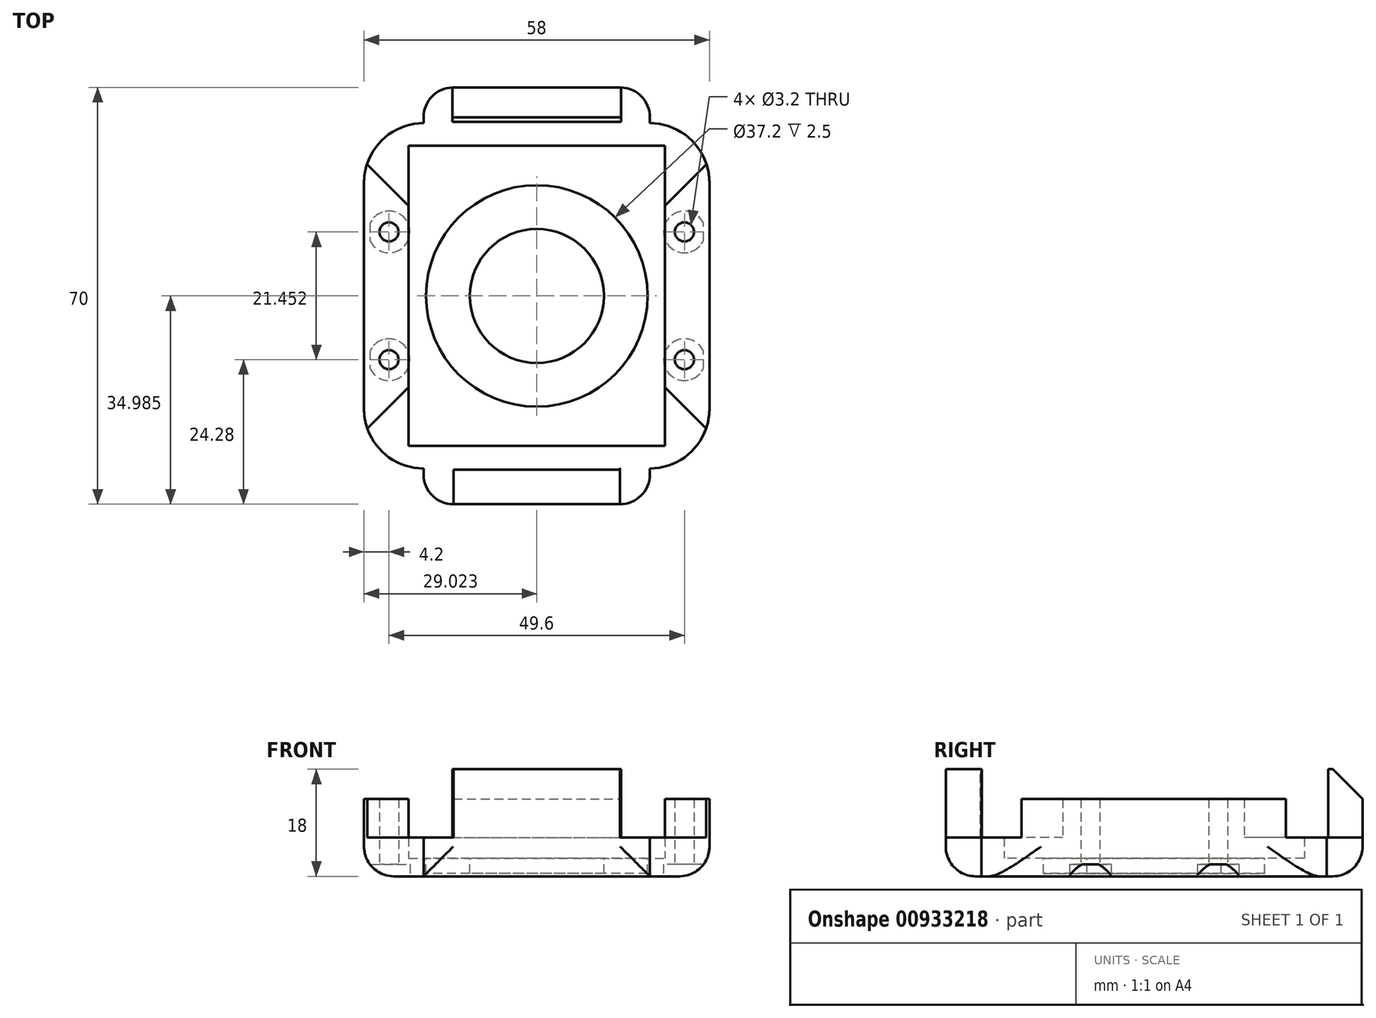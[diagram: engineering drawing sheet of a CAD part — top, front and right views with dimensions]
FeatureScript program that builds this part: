
annotation { "Feature Type Name" : "Feature", "Feature Type Description" : "" }
export const myFeature = defineFeature(function(context is Context, id is Id, definition is map)
    precondition{}
    {
        {
            var Q0;
            Q0=qCreatedBy(makeId("Top.planeOp"),FACE);
            var sketch = newSketch(context, id + "F0", { "sketchPlane" : qUnion([Q0])});
            skPoint(sketch, "E0.middle", {"position": v(-30.2, 30.2) * mm});
            skLineSegment(sketch, "E1", {"start": v(-30.2, 30.2) * mm, "end": v(-30.2, 55.4) * mm});
            skLineSegment(sketch, "E2", {"start": v(-30.2, 55.4) * mm, "end": v(-30.2, 59.2) * mm});
            skLineSegment(sketch, "E3", {"start": v(-30.2, 30.2) * mm, "end": v(-30.2, 5) * mm});
            skLineSegment(sketch, "E4", {"start": v(-30.2, 5) * mm, "end": v(-30.2, 1.2) * mm});
            skLineSegment(sketch, "E5", {"start": v(-30.2, 1.2) * mm, "end": v(-11.2, 1.2) * mm});
            skLineSegment(sketch, "E6", {"start": v(-1.2, 49.2) * mm, "end": v(-1.2, 11.2) * mm});
            skLineSegment(sketch, "E7", {"start": v(-11.2, 59.2) * mm, "end": v(-30.2, 59.2) * mm});
            skLineSegment(sketch, "E8", {"start": v(-8.68, 55.4) * mm, "end": v(-8.68, 5) * mm});
            skLineSegment(sketch, "E9.MirrorCS", {"start": v(-51.73, 55.4) * mm, "end": v(-51.73, 5) * mm});
            skLineSegment(sketch, "E10.MirrorCS", {"start": v(-30.2, 1.2) * mm, "end": v(-49.2, 1.2) * mm});
            skLineSegment(sketch, "E11.MirrorCS", {"start": v(-49.2, 59.2) * mm, "end": v(-30.2, 59.2) * mm});
            skLineSegment(sketch, "E12.MirrorCS", {"start": v(-59.2, 49.2) * mm, "end": v(-59.2, 11.2) * mm});
            skArc(sketch, "E13", {"start": v(-49.2, 59.2) * mm, "mid": v(-56.27, 56.27) * mm, "end": v(-59.2, 49.2) * mm});
            skArc(sketch, "E14", {"start": v(-1.2, 49.2) * mm, "mid": v(-4.13, 56.27) * mm, "end": v(-11.2, 59.2) * mm});
            skArc(sketch, "E15", {"start": v(-11.2, 1.2) * mm, "mid": v(-4.13, 4.13) * mm, "end": v(-1.2, 11.2) * mm});
            skArc(sketch, "E16", {"start": v(-59.2, 11.2) * mm, "mid": v(-56.27, 4.13) * mm, "end": v(-49.2, 1.2) * mm});
            skLineSegment(sketch, "E17", {"start": v(-51.73, 5) * mm, "end": v(-30.2, 5) * mm});
            skLineSegment(sketch, "E18", {"start": v(-30.2, 5) * mm, "end": v(-8.68, 5) * mm});
            skLineSegment(sketch, "E19", {"start": v(-51.73, 55.4) * mm, "end": v(-30.2, 55.4) * mm});
            skLineSegment(sketch, "E20", {"start": v(-8.68, 55.4) * mm, "end": v(-30.2, 55.4) * mm});
            skSolve(sketch);
        }
        {
            var Q0;
            Q0=makeQuery(id+"F0.imprint","IMPRINT",FACE,{"disambiguationData":[TD([[makeQuery(id+"F0.imprint","IMPRINT",EDGE,{"derivedFrom":sQuery(id+"F0.wireOp",EDGE,"E4")}),-1.0]])]});
            var Q1;
            Q1=makeQuery(id+"F0.imprint","IMPRINT",FACE,{"disambiguationData":[TD([[makeQuery(id+"F0.imprint","IMPRINT",EDGE,{"derivedFrom":sQuery(id+"F0.wireOp",EDGE,"GW4XANve-GKL7-1srf-qrfw-00KNjBr2ELYc")}),1.0]])]});
            var Q2;
            Q2=makeQuery(id+"F0.imprint","IMPRINT",FACE,{"disambiguationData":[TD([[makeQuery(id+"F0.imprint","IMPRINT",EDGE,{"derivedFrom":sQuery(id+"F0.wireOp",EDGE,"E5")}),1.0]])]});
            extrude(context, id + "F1", {"entities" : qUnion([Q0, Q1, Q2]), "depth" : 13 * mm, "offsetDistance" : 25 * mm});
        }
        {
            var Q0;
            Q0=makeQuery(id+"F1.opExtrude","CAP_EDGE",EDGE,{"disambiguationData":[OSD([sQuery(id+"F0.wireOp",EDGE,"E6")])],"isStart":true});
            var Q1;
            Q1=makeQuery(id+"F1.opExtrude","CAP_EDGE",EDGE,{"disambiguationData":[OSD([sQuery(id+"F0.wireOp",EDGE,"E12.MirrorCS")])],"isStart":true});
            fillet(context, id + "F2", {"entities" : qUnion([Q0, Q1]), "radius" : 5 * mm, "allowEdgeOverflow" : false});
        }
        {
            var Q0;
            Q0=makeQuery(id+"F0.imprint","IMPRINT",FACE,{"disambiguationData":[TD([[makeQuery(id+"F0.imprint","IMPRINT",EDGE,{"derivedFrom":sQuery(id+"F0.wireOp",EDGE,"E1")}),1.0]])]});
            var Q1;
            Q1=makeQuery(id+"F0.imprint","IMPRINT",FACE,{"disambiguationData":[TD([[makeQuery(id+"F0.imprint","IMPRINT",EDGE,{"derivedFrom":sQuery(id+"F0.wireOp",EDGE,"E1")}),-1.0]])]});
            extrude(context, id + "F3", {"entities" : qUnion([Q0, Q1]), "operationType" : NewBodyOperationType.ADD, "depth" : 3 * mm, "offsetDistance" : 25 * mm});
        }
        {
            var Q0;
            Q0=qCreatedBy(makeId("Top.planeOp"),FACE);
            var sketch = newSketch(context, id + "F4", { "sketchPlane" : qUnion([Q0])});
            skCircle(sketch, "E21", {"center": v(-60.36, 60) * mm, "radius": 3.5 * mm});
            skCircle(sketch, "E22", {"center": v(-60.36, 0) * mm, "radius": 3.5 * mm});
            skCircle(sketch, "E23", {"center": v(-0.4, 60) * mm, "radius": 3.5 * mm});
            skCircle(sketch, "E24", {"center": v(-0.4, 0) * mm, "radius": 3.5 * mm});
            skCircle(sketch, "E25", {"center": v(-60.36, 0) * mm, "radius": 1.6 * mm});
            skCircle(sketch, "E26", {"center": v(-60.36, 60) * mm, "radius": 1.6 * mm});
            skCircle(sketch, "E27", {"center": v(-0.4, 0) * mm, "radius": 1.6 * mm});
            skCircle(sketch, "E28", {"center": v(-0.4, 60) * mm, "radius": 1.6 * mm});
            skCircle(sketch, "E29", {"center": v(-5.4, 40.93) * mm, "radius": 1.6 * mm});
            skCircle(sketch, "E30", {"center": v(-5.4, 19.48) * mm, "radius": 1.6 * mm});
            skCircle(sketch, "E31", {"center": v(-55, 40.93) * mm, "radius": 1.6 * mm});
            skCircle(sketch, "E32", {"center": v(-55, 19.48) * mm, "radius": 1.6 * mm});
            skCircle(sketch, "E33", {"center": v(-55, 40.93) * mm, "radius": 3.5 * mm});
            skCircle(sketch, "E34", {"center": v(-55, 19.48) * mm, "radius": 3.5 * mm});
            skCircle(sketch, "E35", {"center": v(-5.4, 40.93) * mm, "radius": 3.5 * mm});
            skCircle(sketch, "E36", {"center": v(-5.4, 19.48) * mm, "radius": 3.5 * mm});
            skLineSegment(sketch, "E37", {"start": v(-29.99, 1.14) * mm, "end": v(-67.14, 1.14) * mm});
            skCircle(sketch, "E38", {"center": v(-9.99, 9.78) * mm, "radius": 4 * mm});
            skCircle(sketch, "E39", {"center": v(-9.99, 50.33) * mm, "radius": 4 * mm});
            skCircle(sketch, "E40", {"center": v(-50.56, 9.78) * mm, "radius": 4 * mm});
            skCircle(sketch, "E41", {"center": v(-50.56, 50.33) * mm, "radius": 4 * mm});
            skSolve(sketch);
        }
        {
            var Q0;
            Q0=makeQuery(id+"F4.imprint","IMPRINT",FACE,{"disambiguationData":[TD([[makeQuery(id+"F4.imprint","IMPRINT",EDGE,{"derivedFrom":sQuery(id+"F4.wireOp",EDGE,"E23")}),1.0]])]});
            var Q1;
            Q1=makeQuery(id+"F4.imprint","IMPRINT",FACE,{"disambiguationData":[TD([[makeQuery(id+"F4.imprint","IMPRINT",EDGE,{"derivedFrom":sQuery(id+"F4.wireOp",EDGE,"E21")}),1.0]])]});
            var Q2;
            Q2=makeQuery(id+"F4.imprint","IMPRINT",FACE,{"disambiguationData":[TD([[makeQuery(id+"F4.imprint","IMPRINT",EDGE,{"derivedFrom":sQuery(id+"F4.wireOp",EDGE,"E22")}),1.0]])]});
            var Q3;
            Q3=makeQuery(id+"F4.imprint","IMPRINT",FACE,{"disambiguationData":[TD([[makeQuery(id+"F4.imprint","IMPRINT",EDGE,{"derivedFrom":sQuery(id+"F4.wireOp",EDGE,"E24")}),1.0]])]});
            var Q4;
            Q4=makeQuery(id+"F4.imprint","IMPRINT",FACE,{"disambiguationData":[TD([[makeQuery(id+"F4.imprint","IMPRINT",EDGE,{"derivedFrom":sQuery(id+"F4.wireOp",EDGE,"E31")}),-1.0]])]});
            var Q5;
            Q5=makeQuery(id+"F4.imprint","IMPRINT",FACE,{"disambiguationData":[TD([[makeQuery(id+"F4.imprint","IMPRINT",EDGE,{"derivedFrom":sQuery(id+"F4.wireOp",EDGE,"E32")}),-1.0]])]});
            var Q6;
            Q6=makeQuery(id+"F4.imprint","IMPRINT",FACE,{"disambiguationData":[TD([[makeQuery(id+"F4.imprint","IMPRINT",EDGE,{"derivedFrom":sQuery(id+"F4.wireOp",EDGE,"E29")}),-1.0]])]});
            var Q7;
            Q7=makeQuery(id+"F4.imprint","IMPRINT",FACE,{"disambiguationData":[TD([[makeQuery(id+"F4.imprint","IMPRINT",EDGE,{"derivedFrom":sQuery(id+"F4.wireOp",EDGE,"E30")}),-1.0]])]});
            var Q8;
            Q8=sQuery(id+"F4.wireOp",EDGE,"E23");
            extrude(context, id + "F5", {"entities" : qUnion([Q0, Q1, Q2, Q3, Q4, Q5, Q6, Q7]), "operationType" : NewBodyOperationType.REMOVE, "surfaceEntities" : qUnion([Q8]), "depth" : 2 * mm, "offsetDistance" : 25 * mm});
        }
        {
            var Q0;
            Q0=makeQuery(id+"F4.imprint","IMPRINT",FACE,{"disambiguationData":[TD([[makeQuery(id+"F4.imprint","IMPRINT",EDGE,{"derivedFrom":sQuery(id+"F4.wireOp",EDGE,"E27")}),1.0]])]});
            var Q1;
            Q1=makeQuery(id+"F4.imprint","IMPRINT",FACE,{"disambiguationData":[TD([[makeQuery(id+"F4.imprint","IMPRINT",EDGE,{"derivedFrom":sQuery(id+"F4.wireOp",EDGE,"E28")}),1.0]])]});
            var Q2;
            Q2=makeQuery(id+"F4.imprint","IMPRINT",FACE,{"disambiguationData":[TD([[makeQuery(id+"F4.imprint","IMPRINT",EDGE,{"derivedFrom":sQuery(id+"F4.wireOp",EDGE,"E26")}),1.0]])]});
            var Q3;
            Q3=makeQuery(id+"F4.imprint","IMPRINT",FACE,{"disambiguationData":[TD([[makeQuery(id+"F4.imprint","IMPRINT",EDGE,{"derivedFrom":sQuery(id+"F4.wireOp",EDGE,"E25")}),1.0]])]});
            var Q4;
            Q4=makeQuery(id+"F4.imprint","IMPRINT",FACE,{"disambiguationData":[TD([[makeQuery(id+"F4.imprint","IMPRINT",EDGE,{"derivedFrom":sQuery(id+"F4.wireOp",EDGE,"E29")}),1.0]])]});
            var Q5;
            Q5=makeQuery(id+"F4.imprint","IMPRINT",FACE,{"disambiguationData":[TD([[makeQuery(id+"F4.imprint","IMPRINT",EDGE,{"derivedFrom":sQuery(id+"F4.wireOp",EDGE,"E30")}),1.0]])]});
            var Q6;
            Q6=makeQuery(id+"F4.imprint","IMPRINT",FACE,{"disambiguationData":[TD([[makeQuery(id+"F4.imprint","IMPRINT",EDGE,{"derivedFrom":sQuery(id+"F4.wireOp",EDGE,"E32")}),1.0]])]});
            var Q7;
            Q7=makeQuery(id+"F4.imprint","IMPRINT",FACE,{"disambiguationData":[TD([[makeQuery(id+"F4.imprint","IMPRINT",EDGE,{"derivedFrom":sQuery(id+"F4.wireOp",EDGE,"E31")}),1.0]])]});
            extrude(context, id + "F6", {"entities" : qUnion([Q0, Q1, Q2, Q3, Q4, Q5, Q6, Q7]), "operationType" : NewBodyOperationType.REMOVE, "depth" : 25 * mm, "offsetDistance" : 25 * mm});
        }
        {
            var Q0;
            Q0=makeQuery(id+"F3.opExtrude","CAP_FACE",FACE,{"disambiguationData":[OSD([sQuery(id+"F0.wireOp",EDGE,"piOKfCNf-9K0Y-vCMg-MYKp-rQM3WEvo7tjS"),sQuery(id+"F0.wireOp",EDGE,"E8"),sQuery(id+"F0.wireOp",EDGE,"WZ0sFQZI-nBvw-yqqw-dlFr-medNQ8aPjnrY"),sQuery(id+"F0.wireOp",EDGE,"af8eacb0-9355-44b9-9afd-123b7ccd3d5d11.MirrorCS"),sQuery(id+"F0.wireOp",EDGE,"E9.MirrorCS"),sQuery(id+"F0.wireOp",EDGE,"af8eacb0-9355-44b9-9afd-123b7ccd3d5d20.MirrorCS")])],"isStart":false});
            var sketch = newSketch(context, id + "F7", { "sketchPlane" : qUnion([Q0])});
            skCircle(sketch, "E42", {"center": v(-30.18, 30.19) * mm, "radius": 18.6 * mm});
            skCircle(sketch, "E43", {"center": v(-30.18, 30.19) * mm, "radius": 11.25 * mm});
            skSolve(sketch);
        }
        {
            var Q0;
            Q0=makeQuery(id+"F7.imprint","IMPRINT",FACE,{"disambiguationData":[TD([[makeQuery(id+"F7.imprint","IMPRINT",EDGE,{"derivedFrom":sQuery(id+"F7.wireOp",EDGE,"E42")}),1.0]])]});
            extrude(context, id + "F8", {"entities" : qUnion([Q0]), "operationType" : NewBodyOperationType.REMOVE, "oppositeDirection" : true, "depth" : 2.5 * mm, "offsetDistance" : 25 * mm});
        }
        {
            var Q0;
            Q0=makeQuery(id+"F4.imprint","IMPRINT",FACE,{"disambiguationData":[TD([[makeQuery(id+"F4.imprint","IMPRINT",EDGE,{"derivedFrom":sQuery(id+"F4.wireOp",EDGE,"E39")}),1.0]])]});
            var Q1;
            Q1=makeQuery(id+"F4.imprint","IMPRINT",FACE,{"disambiguationData":[TD([[makeQuery(id+"F4.imprint","IMPRINT",EDGE,{"derivedFrom":sQuery(id+"F4.wireOp",EDGE,"E41")}),1.0]])]});
            var Q2;
            Q2=makeQuery(id+"F4.imprint","IMPRINT",FACE,{"disambiguationData":[TD([[makeQuery(id+"F4.imprint","IMPRINT",EDGE,{"derivedFrom":sQuery(id+"F4.wireOp",EDGE,"E40")}),1.0]])]});
            var Q3;
            Q3=makeQuery(id+"F4.imprint","IMPRINT",FACE,{"disambiguationData":[TD([[makeQuery(id+"F4.imprint","IMPRINT",EDGE,{"derivedFrom":sQuery(id+"F4.wireOp",EDGE,"E38")}),1.0]])]});
            extrude(context, id + "F9", {"entities" : qUnion([Q0, Q1, Q2, Q3]), "operationType" : NewBodyOperationType.REMOVE, "depth" : 25 * mm, "offsetDistance" : 25 * mm, "hasSecondDirection" : true, "secondDirectionOppositeDirection" : false, "secondDirectionDepth" : 8 * mm});
        }
        {
            var Q0;
            Q0=qCreatedBy(makeId("Top.planeOp"),FACE);
            var sketch = newSketch(context, id + "F10", { "sketchPlane" : qUnion([Q0])});
            skLineSegment(sketch, "E44.bottom", {"start": v(-60.68, 5.92) * mm, "end": v(-50.07, 16.53) * mm});
            skLineSegment(sketch, "E44.top", {"start": v(-50.07, -4.69) * mm, "end": v(-39.46, 5.92) * mm});
            skLineSegment(sketch, "E44.left", {"start": v(-60.68, 5.92) * mm, "end": v(-50.07, -4.69) * mm});
            skLineSegment(sketch, "E44.right", {"start": v(-50.07, 16.53) * mm, "end": v(-39.46, 5.92) * mm});
            skLineSegment(sketch, "E45", {"start": v(-30, 30.1) * mm, "end": v(-47.81, 30.1) * mm});
            skLineSegment(sketch, "E46.MirrorCS", {"start": v(0.27, 5.92) * mm, "end": v(-10.33, 16.53) * mm});
            skLineSegment(sketch, "E47.MirrorCS", {"start": v(-10.33, -4.69) * mm, "end": v(-20.94, 5.92) * mm});
            skLineSegment(sketch, "E48.MirrorCS", {"start": v(0.27, 5.92) * mm, "end": v(-10.33, -4.69) * mm});
            skLineSegment(sketch, "E49.MirrorCS", {"start": v(-10.33, 16.53) * mm, "end": v(-20.94, 5.92) * mm});
            skLineSegment(sketch, "E50.MirrorCS", {"start": v(-10.33, 43.69) * mm, "end": v(-20.94, 54.3) * mm});
            skLineSegment(sketch, "E51.MirrorCS", {"start": v(-50.07, 64.9) * mm, "end": v(-39.46, 54.3) * mm});
            skLineSegment(sketch, "E52.MirrorCS", {"start": v(-60.68, 54.3) * mm, "end": v(-50.07, 43.69) * mm});
            skLineSegment(sketch, "E53.MirrorCS", {"start": v(0.27, 54.3) * mm, "end": v(-10.33, 43.69) * mm});
            skLineSegment(sketch, "E54.MirrorCS", {"start": v(-10.33, 64.9) * mm, "end": v(-20.94, 54.3) * mm});
            skLineSegment(sketch, "E55.MirrorCS", {"start": v(0.27, 54.3) * mm, "end": v(-10.33, 64.9) * mm});
            skLineSegment(sketch, "E56.MirrorCS", {"start": v(-50.07, 43.69) * mm, "end": v(-39.46, 54.3) * mm});
            skLineSegment(sketch, "E57.MirrorCS", {"start": v(-60.68, 54.3) * mm, "end": v(-50.07, 64.9) * mm});
            skSolve(sketch);
        }
        {
            var Q0;
            Q0=makeQuery(id+"F10.imprint","IMPRINT",FACE,{"disambiguationData":[TD([[makeQuery(id+"F10.imprint","IMPRINT",EDGE,{"derivedFrom":sQuery(id+"F10.wireOp",EDGE,"E44.bottom")}),-1.0]])]});
            var Q1;
            Q1=makeQuery(id+"F10.imprint","IMPRINT",FACE,{"disambiguationData":[TD([[makeQuery(id+"F10.imprint","IMPRINT",EDGE,{"derivedFrom":sQuery(id+"F10.wireOp",EDGE,"bd2f957f-f70f-4264-94f9-0902b26125ed1.MirrorCS")}),1.0]])]});
            var Q2;
            Q2=makeQuery(id+"F10.imprint","IMPRINT",FACE,{"disambiguationData":[TD([[makeQuery(id+"F10.imprint","IMPRINT",EDGE,{"derivedFrom":sQuery(id+"F10.wireOp",EDGE,"bd2f957f-f70f-4264-94f9-0902b26125ed0.MirrorCS")}),1.0]])]});
            var Q3;
            Q3=makeQuery(id+"F10.imprint","IMPRINT",FACE,{"disambiguationData":[TD([[makeQuery(id+"F10.imprint","IMPRINT",EDGE,{"derivedFrom":sQuery(id+"F10.wireOp",EDGE,"9af36c23-f677-4934-87c6-d91073def1bc0.MirrorCS")}),1.0]])]});
            var Q4;
            Q4=makeQuery(id+"F10.imprint","IMPRINT",FACE,{"disambiguationData":[TD([[makeQuery(id+"F10.imprint","IMPRINT",EDGE,{"derivedFrom":sQuery(id+"F10.wireOp",EDGE,"a2501e6f-06cb-41c8-a8cc-c55ed2d7a5468.MirrorCS")}),1.0]])]});
            var Q5;
            Q5=makeQuery(id+"F10.imprint","IMPRINT",FACE,{"disambiguationData":[TD([[makeQuery(id+"F10.imprint","IMPRINT",EDGE,{"derivedFrom":sQuery(id+"F10.wireOp",EDGE,"E44.right")}),-1.0]])]});
            var Q6;
            Q6=makeQuery(id+"F10.imprint","IMPRINT",FACE,{"disambiguationData":[TD([[makeQuery(id+"F10.imprint","IMPRINT",EDGE,{"derivedFrom":sQuery(id+"F10.wireOp",EDGE,"d150f776-ecc3-457d-8fed-678e8fbbb3bf1.MirrorCS")}),1.0]])]});
            var Q7;
            Q7=makeQuery(id+"F10.imprint","IMPRINT",FACE,{"disambiguationData":[TD([[makeQuery(id+"F10.imprint","IMPRINT",EDGE,{"derivedFrom":sQuery(id+"F10.wireOp",EDGE,"a2501e6f-06cb-41c8-a8cc-c55ed2d7a54611.MirrorCS")}),1.0]])]});
            var Q8;
            Q8=makeQuery(id+"F10.imprint","IMPRINT",FACE,{"disambiguationData":[TD([[makeQuery(id+"F10.imprint","IMPRINT",EDGE,{"derivedFrom":sQuery(id+"F10.wireOp",EDGE,"d1094237-c39f-41a1-b04b-d4c12975f0049.MirrorCS")}),1.0]])]});
            var Q9;
            Q9=makeQuery(id+"F10.imprint","IMPRINT",FACE,{"disambiguationData":[TD([[makeQuery(id+"F10.imprint","IMPRINT",EDGE,{"derivedFrom":sQuery(id+"F10.wireOp",EDGE,"d1094237-c39f-41a1-b04b-d4c12975f0048.MirrorCS")}),1.0]])]});
            var Q10;
            Q10=makeQuery(id+"F10.imprint","IMPRINT",FACE,{"disambiguationData":[TD([[makeQuery(id+"F10.imprint","IMPRINT",EDGE,{"derivedFrom":sQuery(id+"F10.wireOp",EDGE,"e9c9b5e1-97b2-4d87-af45-e714632e2cff4.MirrorCS")}),-1.0]])]});
            var Q11;
            Q11=makeQuery(id+"F10.imprint","IMPRINT",FACE,{"disambiguationData":[TD([[makeQuery(id+"F10.imprint","IMPRINT",EDGE,{"derivedFrom":sQuery(id+"F10.wireOp",EDGE,"E47.MirrorCS")}),-1.0]])]});
            var Q12;
            Q12=makeQuery(id+"F10.imprint","IMPRINT",FACE,{"disambiguationData":[TD([[makeQuery(id+"F10.imprint","IMPRINT",EDGE,{"derivedFrom":sQuery(id+"F10.wireOp",EDGE,"E52.MirrorCS")}),1.0]])]});
            var Q13;
            Q13=makeQuery(id+"F10.imprint","IMPRINT",FACE,{"disambiguationData":[TD([[makeQuery(id+"F10.imprint","IMPRINT",EDGE,{"derivedFrom":sQuery(id+"F10.wireOp",EDGE,"E55.MirrorCS")}),1.0]])]});
            extrude(context, id + "F11", {"entities" : qUnion([Q0, Q1, Q2, Q3, Q4, Q5, Q6, Q7, Q8, Q9, Q10, Q11, Q12, Q13]), "operationType" : NewBodyOperationType.REMOVE, "depth" : 13 * mm, "offsetDistance" : 25 * mm, "hasSecondDirection" : true, "secondDirectionOppositeDirection" : false, "secondDirectionDepth" : 6.5 * mm});
        }
        {
            var Q0;
            Q0=makeQuery(id+"F1.opExtrude","SWEPT_FACE",FACE,{"disambiguationData":[OSD([sQuery(id+"F0.wireOp",EDGE,"E7"),sQuery(id+"F0.wireOp",EDGE,"E11.MirrorCS")])]});
            extrude(context, id + "F12", {"entities" : qUnion([Q0]), "operationType" : NewBodyOperationType.ADD, "depth" : 6 * mm, "offsetDistance" : 25 * mm});
        }
        {
            var Q0;
            Q0=makeQuery(id+"F1.opExtrude","SWEPT_FACE",FACE,{"disambiguationData":[OSD([sQuery(id+"F0.wireOp",EDGE,"E5"),sQuery(id+"F0.wireOp",EDGE,"E10.MirrorCS")])]});
            extrude(context, id + "F13", {"entities" : qUnion([Q0]), "operationType" : NewBodyOperationType.ADD, "depth" : 6 * mm, "offsetDistance" : 25 * mm});
        }
        {
            var Q0;
            Q0=makeQuery(id+"F12.opExtrude","CAP_EDGE",EDGE,{"disambiguationData":[OSD([sQuery(id+"F0.wireOp",EDGE,"E7"),sQuery(id+"F0.wireOp",EDGE,"E14")])],"isStart":false});
            var Q1;
            Q1=makeQuery(id+"F12.opExtrude","CAP_EDGE",EDGE,{"disambiguationData":[OSD([sQuery(id+"F0.wireOp",EDGE,"E11.MirrorCS"),sQuery(id+"F0.wireOp",EDGE,"E13")])],"isStart":false});
            var Q2;
            Q2=makeQuery(id+"F13.opExtrude","CAP_EDGE",EDGE,{"disambiguationData":[OSD([sQuery(id+"F0.wireOp",EDGE,"E10.MirrorCS"),sQuery(id+"F0.wireOp",EDGE,"E16")])],"isStart":false});
            var Q3;
            Q3=makeQuery(id+"F13.opExtrude","CAP_EDGE",EDGE,{"disambiguationData":[OSD([sQuery(id+"F0.wireOp",EDGE,"E5"),sQuery(id+"F0.wireOp",EDGE,"E15")])],"isStart":false});
            var Q4;
            {var subQ0=sQuery(id+"F0.wireOp",EDGE,"E10.MirrorCS");var subQ1=sQuery(id+"F0.wireOp",EDGE,"E5");Q4=makeQuery(id+"F13.opExtrude","CAP_EDGE",EDGE,{"disambiguationData":[OSD([subQ1,subQ0]),TDD([makeQuery(id+"F1.opExtrude","CAP_EDGE",EDGE,{"disambiguationData":[OSD([subQ1,subQ0])],"isStart":true})])],"isStart":false});}
            var Q5;
            {var subQ0=sQuery(id+"F0.wireOp",EDGE,"E11.MirrorCS");var subQ1=sQuery(id+"F0.wireOp",EDGE,"E7");Q5=makeQuery(id+"F12.opExtrude","CAP_EDGE",EDGE,{"disambiguationData":[OSD([subQ1,subQ0]),TDD([makeQuery(id+"F1.opExtrude","CAP_EDGE",EDGE,{"disambiguationData":[OSD([subQ1,subQ0])],"isStart":true})])],"isStart":false});}
            fillet(context, id + "F14", {"entities" : qUnion([Q0, Q1, Q2, Q3, Q4, Q5]), "radius" : 5 * mm, "tangentPropagation" : true, "allowEdgeOverflow" : false});
        }
        {
            var Q0;
            Q0=makeQuery(id+"F1.opExtrude","SWEPT_FACE",FACE,{"disambiguationData":[OSD([sQuery(id+"F0.wireOp",EDGE,"E17"),sQuery(id+"F0.wireOp",EDGE,"E18")])]});
            var sketch = newSketch(context, id + "F15", { "sketchPlane" : qUnion([Q0])});
            skPoint(sketch, "E58.firstSnap0", {"position": v(30.2, 13) * mm});
            skLineSegment(sketch, "E58.bottom", {"start": v(44.25, 13) * mm, "end": v(16.27, 13) * mm});
            skLineSegment(sketch, "E58.top", {"start": v(44.25, 6.5) * mm, "end": v(16.27, 6.5) * mm});
            skLineSegment(sketch, "E58.left", {"start": v(44.25, 13) * mm, "end": v(44.25, 6.5) * mm});
            skLineSegment(sketch, "E58.right", {"start": v(16.27, 13) * mm, "end": v(16.27, 6.5) * mm});
            skSolve(sketch);
        }
        {
            var Q0;
            {var subQ4=sQuery(id+"F15.wireOp",EDGE,"E58.right");Q0=makeQuery(id+"F15.imprint","IMPRINT",FACE,{"disambiguationData":[TD([[makeQuery(id+"F15.imprint","IMPRINT",EDGE,{"derivedFrom":subQ4}),1.0]])]});}
            var Q1;
            {var subQ1=makeQuery(id+"F1.opExtrude","SWEPT_FACE",FACE,{"disambiguationData":[OSD([sQuery(id+"F0.wireOp",EDGE,"E17"),sQuery(id+"F0.wireOp",EDGE,"E18")])]});var subQ2=makeQuery(id+"F11.boolean.opBoolean","INTERSECT",EDGE,{"derivedFrom":[subQ1,makeQuery(id+"F11.opExtrude","SWEPT_FACE",FACE,{"disambiguationData":[OSD([sQuery(id+"F10.wireOp",EDGE,"E44.top")])]})]});Q1=makeQuery(id+"F15.imprint","IMPRINT",FACE,{"disambiguationData":[TD([[makeQuery(id+"F15.imprint","IMPRINT",EDGE,{"derivedFrom":subQ2}),1.0]])]});}
            var Q2;
            {var subQ4=sQuery(id+"F15.wireOp",EDGE,"E58.left");Q2=makeQuery(id+"F15.imprint","IMPRINT",FACE,{"disambiguationData":[TD([[makeQuery(id+"F15.imprint","IMPRINT",EDGE,{"derivedFrom":subQ4}),-1.0]])]});}
            extrude(context, id + "F16", {"entities" : qUnion([Q0, Q1, Q2]), "operationType" : NewBodyOperationType.REMOVE, "oppositeDirection" : true, "depth" : 4 * mm, "offsetDistance" : 25 * mm});
        }
        {
            var Q0;
            Q0=makeQuery(id+"F1.opExtrude","SWEPT_FACE",FACE,{"disambiguationData":[OSD([sQuery(id+"F0.wireOp",EDGE,"E19"),sQuery(id+"F0.wireOp",EDGE,"E20")])]});
            var sketch = newSketch(context, id + "F17", { "sketchPlane" : qUnion([Q0])});
            skLineSegment(sketch, "E59.bottom", {"start": v(-44.6, 13.3) * mm, "end": v(-15.87, 13.3) * mm});
            skLineSegment(sketch, "E59.top", {"start": v(-44.6, 6.5) * mm, "end": v(-15.87, 6.5) * mm});
            skLineSegment(sketch, "E59.left", {"start": v(-44.6, 13.3) * mm, "end": v(-44.6, 6.5) * mm});
            skLineSegment(sketch, "E59.right", {"start": v(-15.87, 13.3) * mm, "end": v(-15.87, 6.5) * mm});
            skSolve(sketch);
        }
        {
            var Q0;
            Q0=makeQuery(id+"F17.imprint","IMPRINT",FACE,{"disambiguationData":[TD([[makeQuery(id+"F17.imprint","IMPRINT",EDGE,{"derivedFrom":sQuery(id+"F17.wireOp",EDGE,"E59.bottom")}),-1.0]])]});
            var Q1;
            {var subQ1=sQuery(id+"F0.wireOp",EDGE,"E20");var subQ2=sQuery(id+"F0.wireOp",EDGE,"E19");Q1=makeQuery(id+"F17.imprint","IMPRINT",FACE,{"disambiguationData":[TD([[makeQuery(id+"F17.imprint","IMPRINT",EDGE,{"derivedFrom":makeQuery(id+"F1.opExtrude","CAP_EDGE",EDGE,{"disambiguationData":[OSD([subQ2,subQ1])],"isStart":false})}),-1.0]])]});}
            extrude(context, id + "F18", {"entities" : qUnion([Q0, Q1]), "operationType" : NewBodyOperationType.REMOVE, "oppositeDirection" : true, "depth" : 4 * mm, "offsetDistance" : 25 * mm});
        }
        {
            var Q0;
            {var subQ0=sQuery(id+"F0.wireOp",EDGE,"E11.MirrorCS");var subQ1=sQuery(id+"F0.wireOp",EDGE,"E7");var subQ2=sQuery(id+"F0.wireOp",EDGE,"E20");var subQ3=sQuery(id+"F0.wireOp",EDGE,"E19");Q0=makeQuery(id+"F12.boolean.opBoolean","MERGE",FACE,{"derivedFrom":[makeQuery(id+"F11.boolean.opBoolean","SPLIT",FACE,{"disambiguationData":[TD([makeQuery(id+"F11.opExtrude","SWEPT_FACE",FACE,{"disambiguationData":[OSD([sQuery(id+"F10.wireOp",EDGE,"E51.MirrorCS")])]})])],"derivedFrom":makeQuery(id+"F1.opExtrude","CAP_FACE",FACE,{"disambiguationData":[OSD([sQuery(id+"F0.wireOp",EDGE,"E5"),sQuery(id+"F0.wireOp",EDGE,"E6"),subQ1,sQuery(id+"F0.wireOp",EDGE,"E8"),sQuery(id+"F0.wireOp",EDGE,"E9.MirrorCS"),sQuery(id+"F0.wireOp",EDGE,"E10.MirrorCS"),subQ0,sQuery(id+"F0.wireOp",EDGE,"E12.MirrorCS"),sQuery(id+"F0.wireOp",EDGE,"E13"),sQuery(id+"F0.wireOp",EDGE,"E14"),sQuery(id+"F0.wireOp",EDGE,"E15"),sQuery(id+"F0.wireOp",EDGE,"E16"),sQuery(id+"F0.wireOp",EDGE,"E17"),sQuery(id+"F0.wireOp",EDGE,"E18"),subQ3,subQ2])],"isStart":false})}),makeQuery(id+"F12.opExtrude","SWEPT_FACE",FACE,{"disambiguationData":[OSD([subQ1,subQ0]),TDD([makeQuery(id+"F1.opExtrude","CAP_EDGE",EDGE,{"disambiguationData":[OSD([subQ1,subQ0])],"isStart":false})])]})]});}
            var Q1;
            {var subQ0=sQuery(id+"F0.wireOp",EDGE,"E10.MirrorCS");var subQ1=sQuery(id+"F0.wireOp",EDGE,"E5");var subQ2=sQuery(id+"F0.wireOp",EDGE,"E18");var subQ3=sQuery(id+"F0.wireOp",EDGE,"E17");Q1=makeQuery(id+"F13.boolean.opBoolean","MERGE",FACE,{"derivedFrom":[makeQuery(id+"F11.boolean.opBoolean","SPLIT",FACE,{"disambiguationData":[TD([makeQuery(id+"F11.opExtrude","SWEPT_FACE",FACE,{"disambiguationData":[OSD([sQuery(id+"F10.wireOp",EDGE,"E44.top")])]})])],"derivedFrom":makeQuery(id+"F1.opExtrude","CAP_FACE",FACE,{"disambiguationData":[OSD([subQ1,sQuery(id+"F0.wireOp",EDGE,"E6"),sQuery(id+"F0.wireOp",EDGE,"E7"),sQuery(id+"F0.wireOp",EDGE,"E8"),sQuery(id+"F0.wireOp",EDGE,"E9.MirrorCS"),subQ0,sQuery(id+"F0.wireOp",EDGE,"E11.MirrorCS"),sQuery(id+"F0.wireOp",EDGE,"E12.MirrorCS"),sQuery(id+"F0.wireOp",EDGE,"E13"),sQuery(id+"F0.wireOp",EDGE,"E14"),sQuery(id+"F0.wireOp",EDGE,"E15"),sQuery(id+"F0.wireOp",EDGE,"E16"),subQ3,subQ2,sQuery(id+"F0.wireOp",EDGE,"E19"),sQuery(id+"F0.wireOp",EDGE,"E20")])],"isStart":false})}),makeQuery(id+"F13.opExtrude","SWEPT_FACE",FACE,{"disambiguationData":[OSD([subQ1,subQ0]),TDD([makeQuery(id+"F1.opExtrude","CAP_EDGE",EDGE,{"disambiguationData":[OSD([subQ1,subQ0])],"isStart":false})])]})]});}
            extrude(context, id + "F19", {"entities" : qUnion([Q0, Q1]), "operationType" : NewBodyOperationType.ADD, "depth" : 5 * mm, "offsetDistance" : 25 * mm});
        }
        {
            var Q0;
            Q0=makeQuery(id+"F19.opExtrude","CAP_EDGE",EDGE,{"disambiguationData":[OSD([sQuery(id+"F0.wireOp",EDGE,"E7"),sQuery(id+"F0.wireOp",EDGE,"E11.MirrorCS")])],"isStart":false});
            chamfer(context, id + "F20", {"entities" : qUnion([Q0]), "width" : 5 * mm, "tangentPropagation" : true});
        }
    });
